FCSTD DOCUMENT  (FreeCAD 0.19R0.19.2)
Label: laptopStand004
License: All rights reserved
LicenseURL: http://en.wikipedia.org/wiki/All_rights_reserved
objects: Sketcher::SketchObject×1
note: 1 computed .brp shape members not serialized (recipe doc carries the construction recipe); baked Part::Feature solids carry a one-line shape summary decoded from their .brp

FEATURE [Sketcher::SketchObject] Sketch
  FullyConstrained = false
  sketch-geometry (56):
    g0: LineSegment StartX=-22.9272 StartY=136.221 StartZ=0 EndX=-22.9272 EndY=-103.779 EndZ=0
    g1: LineSegment StartX=-22.9272 StartY=136.221 StartZ=0 EndX=387.073 EndY=136.221 EndZ=0
    g2: LineSegment StartX=66.1121 StartY=95.2117 StartZ=0 EndX=66.1121 EndY=-84.7883 EndZ=0
    g3: LineSegment StartX=66.1121 StartY=95.2117 StartZ=0 EndX=256.112 EndY=95.2117 EndZ=0
    g4: LineSegment StartX=256.112 StartY=83.2117 StartZ=0 EndX=78.1121 EndY=83.2117 EndZ=0
    g5: LineSegment StartX=78.1121 StartY=-84.7883 StartZ=0 EndX=78.1121 EndY=83.2117 EndZ=0
    g6: LineSegment StartX=286.112 StartY=83.2117 StartZ=0 EndX=464.112 EndY=83.2117 EndZ=0
    g7: LineSegment StartX=286.112 StartY=95.2117 StartZ=0 EndX=476.112 EndY=95.2117 EndZ=0
    g8: LineSegment StartX=286.112 StartY=95.2117 StartZ=0 EndX=286.112 EndY=89.2117 EndZ=0
    g9-g13: Circle x5 (B-spline internal-alignment scaffolding for g14; pole/knot coordinates omitted)
    g14: BSplineCurve PolesCount=5 KnotsCount=3 Degree=3 IsPeriodic=0
    g15: GeomPoint X=271.112 Y=85.2117 Z=0
    g16: GeomPoint X=258.112 Y=89.2117 Z=0
    g17: GeomPoint X=271.112 Y=89.2117 Z=0
    g18-g22: Circle x5 (B-spline internal-alignment scaffolding for g23; pole/knot coordinates omitted)
    g23: BSplineCurve PolesCount=5 KnotsCount=3 Degree=3 IsPeriodic=0
    g24: GeomPoint X=271.112 Y=93.2117 Z=0
    g25: GeomPoint X=284.112 Y=89.2117 Z=0
    g26: GeomPoint X=271.112 Y=89.2117 Z=0
    g27: LineSegment StartX=256.112 StartY=95.2117 StartZ=0 EndX=271.112 EndY=95.2117 EndZ=0
    g28: LineSegment StartX=271.112 StartY=93.2117 StartZ=0 EndX=271.112 EndY=95.2117 EndZ=0
    g29: LineSegment StartX=286.112 StartY=83.2117 StartZ=0 EndX=271.112 EndY=83.2117 EndZ=0
    g30: LineSegment StartX=271.112 StartY=85.2117 StartZ=0 EndX=271.112 EndY=83.2117 EndZ=0
    g31: LineSegment StartX=330.212 StartY=114.494 StartZ=0 EndX=508.212 EndY=114.494 EndZ=0
    g32: LineSegment StartX=330.212 StartY=126.494 StartZ=0 EndX=520.212 EndY=126.494 EndZ=0
    g33: LineSegment StartX=330.212 StartY=126.494 StartZ=0 EndX=330.212 EndY=120.494 EndZ=0
    g34-g38: Circle x5 (B-spline internal-alignment scaffolding for g39; pole/knot coordinates omitted)
    g39: BSplineCurve PolesCount=5 KnotsCount=3 Degree=3 IsPeriodic=0
    g40: GeomPoint X=315.212 Y=116.494 Z=0
    g41: GeomPoint X=302.212 Y=120.494 Z=0
    g42: GeomPoint X=315.212 Y=120.494 Z=0
    g43-g47: Circle x5 (B-spline internal-alignment scaffolding for g48; pole/knot coordinates omitted)
    g48: BSplineCurve PolesCount=5 KnotsCount=3 Degree=3 IsPeriodic=0
    g49: GeomPoint X=315.212 Y=124.494 Z=0
    g50: GeomPoint X=328.212 Y=120.494 Z=0
    g51: GeomPoint X=315.212 Y=120.494 Z=0
    g52: LineSegment StartX=300.212 StartY=126.494 StartZ=0 EndX=315.212 EndY=126.494 EndZ=0
    g53: LineSegment StartX=315.212 StartY=124.494 StartZ=0 EndX=315.212 EndY=126.494 EndZ=0
    g54: LineSegment StartX=330.212 StartY=114.494 StartZ=0 EndX=315.212 EndY=114.494 EndZ=0
    g55: LineSegment StartX=315.212 StartY=116.494 StartZ=0 EndX=315.212 EndY=114.494 EndZ=0
  constraints (89):
    c: Vertical(g0)
    c: Distance(g0) = 240
    c: Horizontal(g1)
    c: Distance(g1) = 410
    c: Coincident(g1,g0)
    c: Vertical(g2)
    c: Distance(g2) = 180
    c: Horizontal(g3)
    c: Distance(g3) = 190
    c: Coincident(g3,g2)
    c: Block(g2)
    c: Horizontal(g4)
    c: Vertical(g5)
    c: Coincident(g4,g5)
    c: Block(g4)
    c: Block(g5)
    c: Horizontal(g6)
    c: Horizontal(g7)
    c: Distance(g7) = 190
    c: Distance(g6) = 178
    c: Block(g7)
    c: Coincident(g8,g7)
    c: Vertical(g8)
    c: Distance(g8) = 6
    c: Weight(g9) = 1
    c: Equal(g9, g10-g13) x4
    c: InternalAlignment(g9-g13 -> g14) x5
    c: InternalAlignment(g15,g14)
    c: InternalAlignment(g16,g14)
    c: InternalAlignment(g17,g14)
    c: Weight(g18) = 1
    c: Equal(g18,g19)
    c: Equal(g18,g20)
    c: Coincident(g20,g8)
    c: Equal(g18,g21)
    c: Equal(g18,g22)
    c: InternalAlignment(g18-g22 -> g23) x5
    c: InternalAlignment(g24,g23)
    c: InternalAlignment(g25,g23)
    c: InternalAlignment(g26,g23)
    c: Block(g23)
    c: Block(g14)
    c: Coincident(g27,g3)
    c: Horizontal(g27)
    c: Coincident(g28,g23)
    c: Vertical(g28)
    c: Coincident(g27,g28)
    c: Block(g6)
    c: Coincident(g29,g6)
    c: Horizontal(g29)
    c: Coincident(g30,g14)
    c: Vertical(g30)
    c: Coincident(g30,g29)
    c: Horizontal(g31)
    c: Horizontal(g32)
    c: Equal(g7,g32) = 190
    c: Equal(g6,g31) = 178
    c: Block(g32)
    c: Coincident(g33,g32)
    c: Vertical(g33)
    c: Equal(g8,g33) = 6
    c: Equal(g9,g34) = 1
    c: Equal(g34, g35-g38) x4
    c: InternalAlignment(g34-g38 -> g39) x5
    c: InternalAlignment(g40,g39)
    c: InternalAlignment(g41,g39)
    c: InternalAlignment(g42,g39)
    c: Equal(g18,g43) = 1
    c: Equal(g43,g44)
    c: Equal(g43,g45)
    c: Coincident(g45,g33)
    c: Equal(g43,g46)
    c: Equal(g43,g47)
    c: InternalAlignment(g43-g47 -> g48) x5
    c: InternalAlignment(g49,g48)
    c: InternalAlignment(g50,g48)
    c: InternalAlignment(g51,g48)
    c: Block(g48)
    c: Block(g39)
    c: Horizontal(g52)
    c: Coincident(g53,g48)
    c: Vertical(g53)
    c: Coincident(g52,g53)
    c: Block(g31)
    c: Coincident(g54,g31)
    c: Horizontal(g54)
    c: Coincident(g55,g39)
    c: Vertical(g55)
    c: Coincident(g55,g54)
